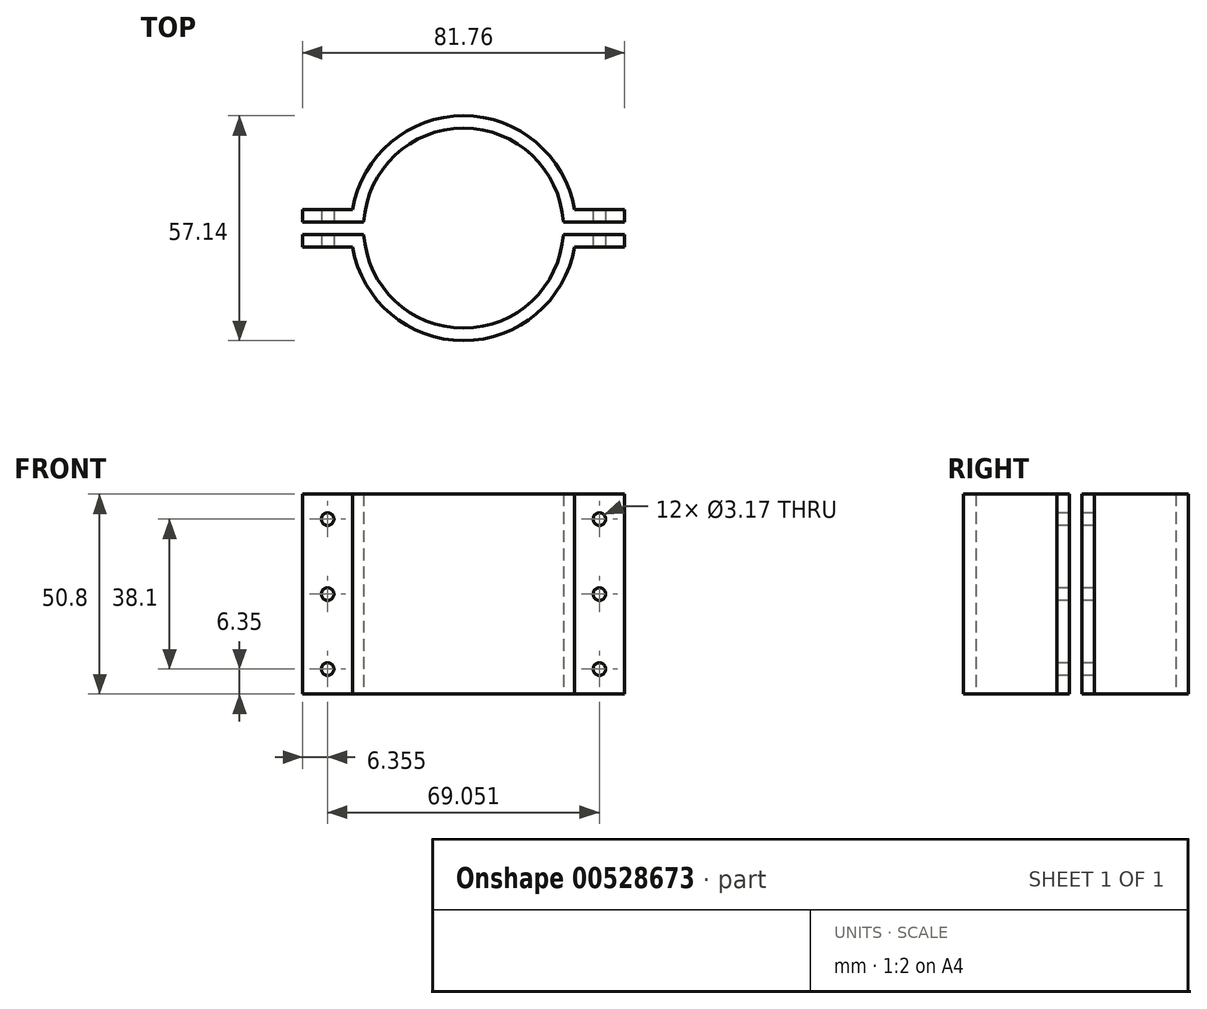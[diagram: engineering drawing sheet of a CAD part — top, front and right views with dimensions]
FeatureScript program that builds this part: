
annotation { "Feature Type Name" : "Feature", "Feature Type Description" : "" }
export const myFeature = defineFeature(function(context is Context, id is Id, definition is map)
    precondition{}
    {
        {
            var Q0;
            Q0=qCreatedBy(makeId("Top.planeOp"),FACE);
            var sketch = newSketch(context, id + "F0", { "sketchPlane" : qUnion([Q0])});
            skArc(sketch, "E0", {"start": v(-25.35, -1.59) * mm, "mid": v(0, -25.4) * mm, "end": v(25.35, -1.59) * mm});
            skArc(sketch, "E1", {"start": v(-28.18, -4.76) * mm, "mid": v(0, -28.58) * mm, "end": v(28.18, -4.76) * mm});
            skLineSegment(sketch, "E2", {"start": v(-40.88, 1.59) * mm, "end": v(-25.35, 1.59) * mm});
            skLineSegment(sketch, "E3", {"start": v(-40.88, -1.59) * mm, "end": v(-25.35, -1.59) * mm});
            skPoint(sketch, "E4.orphan", {"position": v(-25.4, 0) * mm});
            skLineSegment(sketch, "E5.MirrorCS", {"start": v(40.88, 1.59) * mm, "end": v(25.35, 1.59) * mm});
            skLineSegment(sketch, "E6.MirrorCS", {"start": v(40.88, -1.59) * mm, "end": v(25.35, -1.59) * mm});
            skArc(sketch, "E7.trimOffspring", {"start": v(28.18, 4.76) * mm, "mid": v(0, 28.58) * mm, "end": v(-28.18, 4.76) * mm});
            skArc(sketch, "E8.trimOffspring", {"start": v(25.35, 1.59) * mm, "mid": v(0, 25.4) * mm, "end": v(-25.35, 1.59) * mm});
            skLineSegment(sketch, "E9", {"start": v(-40.88, 1.59) * mm, "end": v(-40.88, 4.76) * mm});
            skLineSegment(sketch, "E10", {"start": v(-40.88, 4.76) * mm, "end": v(-28.18, 4.76) * mm});
            skLineSegment(sketch, "E11", {"start": v(-40.88, -1.59) * mm, "end": v(-40.88, -4.76) * mm});
            skLineSegment(sketch, "E12", {"start": v(-40.88, -4.76) * mm, "end": v(-28.18, -4.76) * mm});
            skPoint(sketch, "E13.start.orphan", {"position": v(-37.2, 0) * mm});
            skLineSegment(sketch, "E14.MirrorCS", {"start": v(40.88, 4.76) * mm, "end": v(28.18, 4.76) * mm});
            skLineSegment(sketch, "E15.MirrorCS", {"start": v(40.88, 1.59) * mm, "end": v(40.88, 4.76) * mm});
            skLineSegment(sketch, "E16.MirrorCS", {"start": v(40.88, -1.59) * mm, "end": v(40.88, -4.76) * mm});
            skLineSegment(sketch, "E17.MirrorCS", {"start": v(40.88, -4.76) * mm, "end": v(28.18, -4.76) * mm});
            skPoint(sketch, "E18.MirrorCS.end.orphan", {"position": v(40.88, 1.59) * mm});
            skPoint(sketch, "E18.MirrorCS.start.orphan", {"position": v(37.2, 0) * mm});
            skPoint(sketch, "E19.MirrorCS.end.orphan", {"position": v(40.88, -1.59) * mm});
            skSolve(sketch);
        }
        {
            var Q0;
            Q0 = qSketchRegion(id + "F0", true);
            extrude(context, id + "F1", {"entities" : qUnion([Q0]), "depth" : 50.8 * mm, "offsetDistance" : 25.4 * mm});
        }
        {
            var Q0;
            Q0=makeQuery(id+"F1.opExtrude","SWEPT_FACE",FACE,{"disambiguationData":[OSD([sQuery(id+"F0.wireOp",EDGE,"E17.MirrorCS")])]});
            var sketch = newSketch(context, id + "F2", { "sketchPlane" : qUnion([Q0])});
            skCircle(sketch, "E20", {"center": v(34.53, 44.45) * mm, "radius": 1.59 * mm});
            skCircle(sketch, "E21.0.1.0", {"center": v(34.53, 25.4) * mm, "radius": 1.59 * mm});
            skCircle(sketch, "E21.0.2.0", {"center": v(34.53, 6.35) * mm, "radius": 1.59 * mm});
            skLineSegment(sketch, "E21.direction1", {"start": v(34.53, 44.45) * mm, "end": v(9.13, 44.45) * mm, "construction": true});
            skLineSegment(sketch, "E21.direction2", {"start": v(34.53, 44.45) * mm, "end": v(34.53, 25.4) * mm, "construction": true});
            skCircle(sketch, "E22.MirrorC", {"center": v(-34.53, 25.4) * mm, "radius": 1.59 * mm});
            skCircle(sketch, "E23.MirrorC", {"center": v(-34.53, 6.35) * mm, "radius": 1.59 * mm});
            skCircle(sketch, "E24.MirrorC", {"center": v(-34.53, 44.45) * mm, "radius": 1.59 * mm});
            skSolve(sketch);
        }
        {
            var Q0;
            Q0 = qSketchRegion(id + "F2", true);
            var Q1;
            Q1=makeQuery(id+"F1.opExtrude","SWEPT_FACE",FACE,{"disambiguationData":[OSD([sQuery(id+"F0.wireOp",EDGE,"E14.MirrorCS")])]});
            extrude(context, id + "F3", {"entities" : qUnion([Q0]), "operationType" : NewBodyOperationType.REMOVE, "endBound" : BoundingType.THROUGH_ALL, "oppositeDirection" : true, "depth" : 25.4 * mm, "endBoundEntityFace" : qUnion([Q1]), "offsetDistance" : 25.4 * mm});
        }
    });
